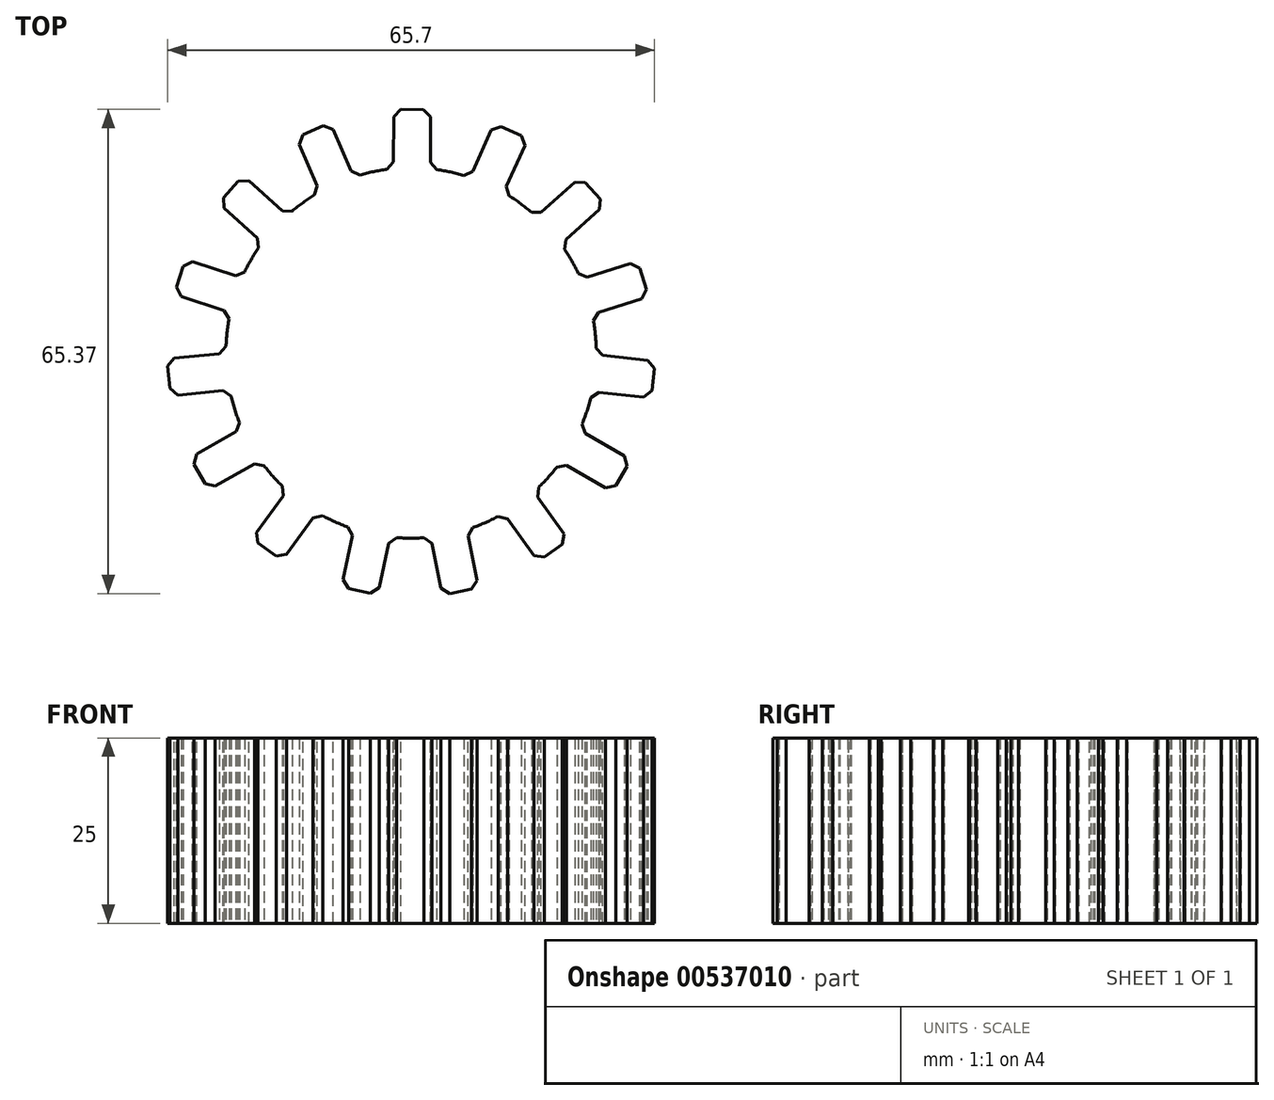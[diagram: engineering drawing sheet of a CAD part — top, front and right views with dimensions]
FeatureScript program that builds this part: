
annotation { "Feature Type Name" : "Feature", "Feature Type Description" : "" }
export const myFeature = defineFeature(function(context is Context, id is Id, definition is map)
    precondition{}
    {
        {
            var Q0;
            Q0=qCreatedBy(makeId("Top.planeOp"),FACE);
            var sketch = newSketch(context, id + "F0", { "sketchPlane" : qUnion([Q0])});
            skArc(sketch, "E0", {"start": v(22.93, 9.96) * mm, "mid": v(21.7, 12.4) * mm, "end": v(20.23, 14.7) * mm});
            skLineSegment(sketch, "E1.bottom", {"start": v(-32.46, -5.77) * mm, "end": v(-32.96, -0.8) * mm});
            skLineSegment(sketch, "E1.top", {"start": v(-24.5, -4.97) * mm, "end": v(-25, 0) * mm, "construction": true});
            skLineSegment(sketch, "E1.left", {"start": v(-32.46, -5.77) * mm, "end": v(-24.5, -4.97) * mm});
            skLineSegment(sketch, "E1.right", {"start": v(-32.96, -0.8) * mm, "end": v(-25, 0) * mm});
            skLineSegment(sketch, "E2.1.0", {"start": v(-27.3, -18.48) * mm, "end": v(-29.78, -14.14) * mm});
            skLineSegment(sketch, "E2.1.1", {"start": v(-27.3, -18.48) * mm, "end": v(-20.36, -14.5) * mm});
            skLineSegment(sketch, "E2.1.2", {"start": v(-29.78, -14.14) * mm, "end": v(-22.84, -10.17) * mm});
            skLineSegment(sketch, "E2.1.3", {"start": v(-20.36, -14.5) * mm, "end": v(-22.84, -10.17) * mm, "construction": true});
            skLineSegment(sketch, "E2.2.0", {"start": v(-17.43, -27.99) * mm, "end": v(-21.46, -25.03) * mm});
            skLineSegment(sketch, "E2.2.1", {"start": v(-17.43, -27.99) * mm, "end": v(-12.7, -21.54) * mm});
            skLineSegment(sketch, "E2.2.2", {"start": v(-21.46, -25.03) * mm, "end": v(-16.73, -18.58) * mm});
            skLineSegment(sketch, "E2.3.0", {"start": v(-4.54, -32.66) * mm, "end": v(-9.42, -31.6) * mm});
            skLineSegment(sketch, "E2.3.1", {"start": v(-4.54, -32.66) * mm, "end": v(-2.84, -24.84) * mm});
            skLineSegment(sketch, "E2.3.2", {"start": v(-9.42, -31.6) * mm, "end": v(-7.73, -23.78) * mm});
            skLineSegment(sketch, "E2.4.0", {"start": v(9.14, -31.68) * mm, "end": v(4.24, -32.7) * mm});
            skLineSegment(sketch, "E2.4.1", {"start": v(9.14, -31.68) * mm, "end": v(7.5, -23.85) * mm});
            skLineSegment(sketch, "E2.4.2", {"start": v(4.24, -32.7) * mm, "end": v(2.61, -24.86) * mm});
            skLineSegment(sketch, "E2.5.0", {"start": v(21.23, -25.22) * mm, "end": v(17.17, -28.14) * mm});
            skLineSegment(sketch, "E2.5.1", {"start": v(21.23, -25.22) * mm, "end": v(16.56, -18.73) * mm});
            skLineSegment(sketch, "E2.5.2", {"start": v(17.17, -28.14) * mm, "end": v(12.5, -21.65) * mm});
            skLineSegment(sketch, "E2.6.0", {"start": v(29.66, -14.4) * mm, "end": v(27.14, -18.73) * mm});
            skLineSegment(sketch, "E2.6.1", {"start": v(29.66, -14.4) * mm, "end": v(22.75, -10.38) * mm});
            skLineSegment(sketch, "E2.6.2", {"start": v(27.14, -18.73) * mm, "end": v(20.23, -14.7) * mm});
            skLineSegment(sketch, "E2.7.0", {"start": v(32.95, -1.1) * mm, "end": v(32.4, -6.07) * mm});
            skLineSegment(sketch, "E2.7.1", {"start": v(32.95, -1.1) * mm, "end": v(25, -0.23) * mm});
            skLineSegment(sketch, "E2.7.2", {"start": v(32.4, -6.07) * mm, "end": v(24.45, -5.2) * mm});
            skLineSegment(sketch, "E2.8.0", {"start": v(30.55, 12.4) * mm, "end": v(32.07, 7.64) * mm});
            skLineSegment(sketch, "E2.8.1", {"start": v(30.55, 12.4) * mm, "end": v(22.93, 9.96) * mm});
            skLineSegment(sketch, "E2.8.2", {"start": v(32.07, 7.64) * mm, "end": v(24.45, 5.2) * mm});
            skLineSegment(sketch, "E2.9.0", {"start": v(22.87, 23.75) * mm, "end": v(26.2, 20.02) * mm});
            skLineSegment(sketch, "E2.9.1", {"start": v(22.87, 23.75) * mm, "end": v(16.9, 18.43) * mm});
            skLineSegment(sketch, "E2.9.2", {"start": v(26.2, 20.02) * mm, "end": v(20.23, 14.7) * mm});
            skLineSegment(sketch, "E2.10.0", {"start": v(11.23, 31) * mm, "end": v(15.79, 28.94) * mm});
            skLineSegment(sketch, "E2.10.1", {"start": v(11.23, 31) * mm, "end": v(7.94, 23.7) * mm});
            skLineSegment(sketch, "E2.10.2", {"start": v(15.79, 28.94) * mm, "end": v(12.5, 21.65) * mm});
            skLineSegment(sketch, "E2.11.0", {"start": v(-2.35, 32.89) * mm, "end": v(2.65, 32.86) * mm});
            skLineSegment(sketch, "E2.11.1", {"start": v(-2.35, 32.89) * mm, "end": v(-2.39, 24.89) * mm});
            skLineSegment(sketch, "E2.11.2", {"start": v(2.65, 32.86) * mm, "end": v(2.61, 24.86) * mm});
            skLineSegment(sketch, "E2.12.0", {"start": v(-15.52, 29.09) * mm, "end": v(-10.95, 31.1) * mm});
            skLineSegment(sketch, "E2.12.1", {"start": v(-15.52, 29.09) * mm, "end": v(-12.3, 21.76) * mm});
            skLineSegment(sketch, "E2.12.2", {"start": v(-10.95, 31.1) * mm, "end": v(-7.73, 23.78) * mm});
            skLineSegment(sketch, "E2.13.0", {"start": v(-26.01, 20.26) * mm, "end": v(-22.65, 23.96) * mm});
            skLineSegment(sketch, "E2.13.1", {"start": v(-26.01, 20.26) * mm, "end": v(-20.1, 14.88) * mm});
            skLineSegment(sketch, "E2.13.2", {"start": v(-22.65, 23.96) * mm, "end": v(-16.73, 18.58) * mm});
            skLineSegment(sketch, "E2.14.0", {"start": v(-32, 7.93) * mm, "end": v(-30.44, 12.68) * mm});
            skLineSegment(sketch, "E2.14.1", {"start": v(-32, 7.93) * mm, "end": v(-24.4, 5.42) * mm});
            skLineSegment(sketch, "E2.14.2", {"start": v(-30.44, 12.68) * mm, "end": v(-22.84, 10.17) * mm});
            skArc(sketch, "E3.trimOffspring", {"start": v(16.9, 18.43) * mm, "mid": v(14.79, 20.16) * mm, "end": v(12.5, 21.65) * mm});
            skArc(sketch, "E4.trimOffspring", {"start": v(7.94, 23.7) * mm, "mid": v(5.3, 24.43) * mm, "end": v(2.61, 24.86) * mm});
            skArc(sketch, "E5.trimOffspring", {"start": v(-2.39, 24.89) * mm, "mid": v(-5.09, 24.48) * mm, "end": v(-7.73, 23.78) * mm});
            skArc(sketch, "E6.trimOffspring", {"start": v(-12.3, 21.76) * mm, "mid": v(-14.6, 20.3) * mm, "end": v(-16.73, 18.58) * mm});
            skArc(sketch, "E7.trimOffspring", {"start": v(-20.1, 14.88) * mm, "mid": v(-21.6, 12.6) * mm, "end": v(-22.84, 10.17) * mm});
            skArc(sketch, "E8.trimOffspring", {"start": v(-24.4, 5.42) * mm, "mid": v(-24.85, 2.73) * mm, "end": v(-25, 0) * mm});
            skArc(sketch, "E9.trimOffspring", {"start": v(-20.36, -14.5) * mm, "mid": v(-18.65, -16.64) * mm, "end": v(-16.73, -18.58) * mm});
            skArc(sketch, "E10.trimOffspring", {"start": v(-12.7, -21.54) * mm, "mid": v(-10.27, -22.8) * mm, "end": v(-7.73, -23.78) * mm});
            skArc(sketch, "E11.trimOffspring", {"start": v(-2.84, -24.84) * mm, "mid": v(-0.11, -25) * mm, "end": v(2.61, -24.86) * mm});
            skArc(sketch, "E12.trimOffspring", {"start": v(7.5, -23.85) * mm, "mid": v(10.06, -22.88) * mm, "end": v(12.5, -21.65) * mm});
            skArc(sketch, "E13.trimOffspring", {"start": v(16.56, -18.73) * mm, "mid": v(18.5, -16.81) * mm, "end": v(20.23, -14.7) * mm});
            skArc(sketch, "E14.trimOffspring", {"start": v(22.75, -10.38) * mm, "mid": v(23.74, -7.83) * mm, "end": v(24.45, -5.2) * mm});
            skArc(sketch, "E15.trimOffspring", {"start": v(25, -0.23) * mm, "mid": v(24.87, 2.5) * mm, "end": v(24.45, 5.2) * mm});
            skArc(sketch, "E16.trimOffspring", {"start": v(-24.5, -4.97) * mm, "mid": v(-23.81, -7.62) * mm, "end": v(-22.84, -10.17) * mm});
            skSolve(sketch);
        }
        {
            var Q0;
            Q0=makeQuery(id+"F0.imprint","IMPRINT",FACE,{"disambiguationData":[TD([[makeQuery(id+"F0.imprint","IMPRINT",EDGE,{"derivedFrom":sQuery(id+"F0.wireOp",EDGE,"E0")}),1.0]])]});
            extrude(context, id + "F1", {"entities" : qUnion([Q0]), "depth" : 25 * mm, "offsetDistance" : 25 * mm});
        }
        {
            var Q0;
            Q0=makeQuery(id+"F1.opExtrude","SWEPT_EDGE",EDGE,{"disambiguationData":[OSD([sQuery(id+"F0.wireOp",EDGE,"E2.1.0"),sQuery(id+"F0.wireOp",EDGE,"E2.1.1")])]});
            var Q1;
            Q1=makeQuery(id+"F1.opExtrude","SWEPT_EDGE",EDGE,{"disambiguationData":[OSD([sQuery(id+"F0.wireOp",EDGE,"E2.2.0"),sQuery(id+"F0.wireOp",EDGE,"E2.2.1")])]});
            var Q2;
            Q2=makeQuery(id+"F1.opExtrude","SWEPT_EDGE",EDGE,{"disambiguationData":[OSD([sQuery(id+"F0.wireOp",EDGE,"E2.3.0"),sQuery(id+"F0.wireOp",EDGE,"E2.3.1")])]});
            var Q3;
            Q3=makeQuery(id+"F1.opExtrude","SWEPT_EDGE",EDGE,{"disambiguationData":[OSD([sQuery(id+"F0.wireOp",EDGE,"E2.4.0"),sQuery(id+"F0.wireOp",EDGE,"E2.4.1")])]});
            var Q4;
            Q4=makeQuery(id+"F1.opExtrude","SWEPT_EDGE",EDGE,{"disambiguationData":[OSD([sQuery(id+"F0.wireOp",EDGE,"E2.4.0"),sQuery(id+"F0.wireOp",EDGE,"E2.4.2")])]});
            var Q5;
            Q5=makeQuery(id+"F1.opExtrude","SWEPT_EDGE",EDGE,{"disambiguationData":[OSD([sQuery(id+"F0.wireOp",EDGE,"E2.3.0"),sQuery(id+"F0.wireOp",EDGE,"E2.3.2")])]});
            var Q6;
            Q6=makeQuery(id+"F1.opExtrude","SWEPT_EDGE",EDGE,{"disambiguationData":[OSD([sQuery(id+"F0.wireOp",EDGE,"E2.2.0"),sQuery(id+"F0.wireOp",EDGE,"E2.2.2")])]});
            var Q7;
            Q7=makeQuery(id+"F1.opExtrude","SWEPT_EDGE",EDGE,{"disambiguationData":[OSD([sQuery(id+"F0.wireOp",EDGE,"E2.5.0"),sQuery(id+"F0.wireOp",EDGE,"E2.5.2")])]});
            var Q8;
            Q8=makeQuery(id+"F1.opExtrude","SWEPT_EDGE",EDGE,{"disambiguationData":[OSD([sQuery(id+"F0.wireOp",EDGE,"E2.5.0"),sQuery(id+"F0.wireOp",EDGE,"E2.5.1")])]});
            var Q9;
            Q9=makeQuery(id+"F1.opExtrude","SWEPT_EDGE",EDGE,{"disambiguationData":[OSD([sQuery(id+"F0.wireOp",EDGE,"E2.6.0"),sQuery(id+"F0.wireOp",EDGE,"E2.6.2")])]});
            var Q10;
            Q10=makeQuery(id+"F1.opExtrude","SWEPT_EDGE",EDGE,{"disambiguationData":[OSD([sQuery(id+"F0.wireOp",EDGE,"E2.6.0"),sQuery(id+"F0.wireOp",EDGE,"E2.6.1")])]});
            var Q11;
            Q11=makeQuery(id+"F1.opExtrude","SWEPT_EDGE",EDGE,{"disambiguationData":[OSD([sQuery(id+"F0.wireOp",EDGE,"E2.7.0"),sQuery(id+"F0.wireOp",EDGE,"E2.7.2")])]});
            var Q12;
            Q12=makeQuery(id+"F1.opExtrude","SWEPT_EDGE",EDGE,{"disambiguationData":[OSD([sQuery(id+"F0.wireOp",EDGE,"E2.7.0"),sQuery(id+"F0.wireOp",EDGE,"E2.7.1")])]});
            var Q13;
            Q13=makeQuery(id+"F1.opExtrude","SWEPT_EDGE",EDGE,{"disambiguationData":[OSD([sQuery(id+"F0.wireOp",EDGE,"E2.8.0"),sQuery(id+"F0.wireOp",EDGE,"E2.8.2")])]});
            var Q14;
            Q14=makeQuery(id+"F1.opExtrude","SWEPT_EDGE",EDGE,{"disambiguationData":[OSD([sQuery(id+"F0.wireOp",EDGE,"E2.8.0"),sQuery(id+"F0.wireOp",EDGE,"E2.8.1")])]});
            var Q15;
            Q15=makeQuery(id+"F1.opExtrude","SWEPT_EDGE",EDGE,{"disambiguationData":[OSD([sQuery(id+"F0.wireOp",EDGE,"E2.9.0"),sQuery(id+"F0.wireOp",EDGE,"E2.9.2")])]});
            var Q16;
            Q16=makeQuery(id+"F1.opExtrude","SWEPT_EDGE",EDGE,{"disambiguationData":[OSD([sQuery(id+"F0.wireOp",EDGE,"E2.9.0"),sQuery(id+"F0.wireOp",EDGE,"E2.9.1")])]});
            var Q17;
            Q17=makeQuery(id+"F1.opExtrude","SWEPT_EDGE",EDGE,{"disambiguationData":[OSD([sQuery(id+"F0.wireOp",EDGE,"E2.10.0"),sQuery(id+"F0.wireOp",EDGE,"E2.10.2")])]});
            var Q18;
            Q18=makeQuery(id+"F1.opExtrude","SWEPT_EDGE",EDGE,{"disambiguationData":[OSD([sQuery(id+"F0.wireOp",EDGE,"E2.10.0"),sQuery(id+"F0.wireOp",EDGE,"E2.10.1")])]});
            var Q19;
            Q19=makeQuery(id+"F1.opExtrude","SWEPT_EDGE",EDGE,{"disambiguationData":[OSD([sQuery(id+"F0.wireOp",EDGE,"E2.11.0"),sQuery(id+"F0.wireOp",EDGE,"E2.11.2")])]});
            var Q20;
            Q20=makeQuery(id+"F1.opExtrude","SWEPT_EDGE",EDGE,{"disambiguationData":[OSD([sQuery(id+"F0.wireOp",EDGE,"E2.11.0"),sQuery(id+"F0.wireOp",EDGE,"E2.11.1")])]});
            var Q21;
            Q21=makeQuery(id+"F1.opExtrude","SWEPT_EDGE",EDGE,{"disambiguationData":[OSD([sQuery(id+"F0.wireOp",EDGE,"E2.12.0"),sQuery(id+"F0.wireOp",EDGE,"E2.12.2")])]});
            var Q22;
            Q22=makeQuery(id+"F1.opExtrude","SWEPT_EDGE",EDGE,{"disambiguationData":[OSD([sQuery(id+"F0.wireOp",EDGE,"E2.12.0"),sQuery(id+"F0.wireOp",EDGE,"E2.12.1")])]});
            var Q23;
            Q23=makeQuery(id+"F1.opExtrude","SWEPT_EDGE",EDGE,{"disambiguationData":[OSD([sQuery(id+"F0.wireOp",EDGE,"E2.13.0"),sQuery(id+"F0.wireOp",EDGE,"E2.13.2")])]});
            var Q24;
            Q24=makeQuery(id+"F1.opExtrude","SWEPT_EDGE",EDGE,{"disambiguationData":[OSD([sQuery(id+"F0.wireOp",EDGE,"E2.13.0"),sQuery(id+"F0.wireOp",EDGE,"E2.13.1")])]});
            var Q25;
            Q25=makeQuery(id+"F1.opExtrude","SWEPT_EDGE",EDGE,{"disambiguationData":[OSD([sQuery(id+"F0.wireOp",EDGE,"E2.14.0"),sQuery(id+"F0.wireOp",EDGE,"E2.14.2")])]});
            var Q26;
            Q26=makeQuery(id+"F1.opExtrude","SWEPT_EDGE",EDGE,{"disambiguationData":[OSD([sQuery(id+"F0.wireOp",EDGE,"E2.14.0"),sQuery(id+"F0.wireOp",EDGE,"E2.14.1")])]});
            var Q27;
            Q27=makeQuery(id+"F1.opExtrude","SWEPT_EDGE",EDGE,{"disambiguationData":[OSD([sQuery(id+"F0.wireOp",EDGE,"E1.bottom"),sQuery(id+"F0.wireOp",EDGE,"E1.right")])]});
            var Q28;
            Q28=makeQuery(id+"F1.opExtrude","SWEPT_EDGE",EDGE,{"disambiguationData":[OSD([sQuery(id+"F0.wireOp",EDGE,"E1.bottom"),sQuery(id+"F0.wireOp",EDGE,"E1.left")])]});
            var Q29;
            Q29=makeQuery(id+"F1.opExtrude","SWEPT_EDGE",EDGE,{"disambiguationData":[OSD([sQuery(id+"F0.wireOp",EDGE,"E2.1.0"),sQuery(id+"F0.wireOp",EDGE,"E2.1.2")])]});
            chamfer(context, id + "F2", {"entities" : qUnion([Q0, Q1, Q2, Q3, Q4, Q5, Q6, Q7, Q8, Q9, Q10, Q11, Q12, Q13, Q14, Q15, Q16, Q17, Q18, Q19, Q20, Q21, Q22, Q23, Q24, Q25, Q26, Q27, Q28, Q29]), "width" : 1 * mm, "tangentPropagation" : true});
        }
        {
            var Q0;
            Q0=makeQuery(id+"F1.opExtrude","SWEPT_EDGE",EDGE,{"disambiguationData":[OSD([sQuery(id+"F0.wireOp",EDGE,"E2.8.2"),sQuery(id+"F0.wireOp",EDGE,"E15.trimOffspring")])]});
            var Q1;
            Q1=makeQuery(id+"F1.opExtrude","SWEPT_EDGE",EDGE,{"disambiguationData":[OSD([sQuery(id+"F0.wireOp",EDGE,"E0"),sQuery(id+"F0.wireOp",EDGE,"E2.9.2")])]});
            var Q2;
            Q2=makeQuery(id+"F1.opExtrude","SWEPT_EDGE",EDGE,{"disambiguationData":[OSD([sQuery(id+"F0.wireOp",EDGE,"E2.10.2"),sQuery(id+"F0.wireOp",EDGE,"E3.trimOffspring")])]});
            var Q3;
            Q3=makeQuery(id+"F1.opExtrude","SWEPT_EDGE",EDGE,{"disambiguationData":[OSD([sQuery(id+"F0.wireOp",EDGE,"E2.11.2"),sQuery(id+"F0.wireOp",EDGE,"E4.trimOffspring")])]});
            var Q4;
            Q4=makeQuery(id+"F1.opExtrude","SWEPT_EDGE",EDGE,{"disambiguationData":[OSD([sQuery(id+"F0.wireOp",EDGE,"E2.12.2"),sQuery(id+"F0.wireOp",EDGE,"E5.trimOffspring")])]});
            var Q5;
            Q5=makeQuery(id+"F1.opExtrude","SWEPT_EDGE",EDGE,{"disambiguationData":[OSD([sQuery(id+"F0.wireOp",EDGE,"E2.13.2"),sQuery(id+"F0.wireOp",EDGE,"E6.trimOffspring")])]});
            var Q6;
            Q6=makeQuery(id+"F1.opExtrude","SWEPT_EDGE",EDGE,{"disambiguationData":[OSD([sQuery(id+"F0.wireOp",EDGE,"E2.14.2"),sQuery(id+"F0.wireOp",EDGE,"E7.trimOffspring")])]});
            var Q7;
            Q7=makeQuery(id+"F1.opExtrude","SWEPT_EDGE",EDGE,{"disambiguationData":[OSD([sQuery(id+"F0.wireOp",EDGE,"E1.right"),sQuery(id+"F0.wireOp",EDGE,"E8.trimOffspring")])]});
            var Q8;
            Q8=makeQuery(id+"F1.opExtrude","SWEPT_EDGE",EDGE,{"disambiguationData":[OSD([sQuery(id+"F0.wireOp",EDGE,"E2.1.2"),sQuery(id+"F0.wireOp",EDGE,"E16.trimOffspring")])]});
            var Q9;
            Q9=makeQuery(id+"F1.opExtrude","SWEPT_EDGE",EDGE,{"disambiguationData":[OSD([sQuery(id+"F0.wireOp",EDGE,"E1.left"),sQuery(id+"F0.wireOp",EDGE,"E16.trimOffspring")])]});
            var Q10;
            Q10=makeQuery(id+"F1.opExtrude","SWEPT_EDGE",EDGE,{"disambiguationData":[OSD([sQuery(id+"F0.wireOp",EDGE,"E2.14.1"),sQuery(id+"F0.wireOp",EDGE,"E8.trimOffspring")])]});
            var Q11;
            Q11=makeQuery(id+"F1.opExtrude","SWEPT_EDGE",EDGE,{"disambiguationData":[OSD([sQuery(id+"F0.wireOp",EDGE,"E2.13.1"),sQuery(id+"F0.wireOp",EDGE,"E7.trimOffspring")])]});
            var Q12;
            Q12=makeQuery(id+"F1.opExtrude","SWEPT_EDGE",EDGE,{"disambiguationData":[OSD([sQuery(id+"F0.wireOp",EDGE,"E2.1.1"),sQuery(id+"F0.wireOp",EDGE,"E9.trimOffspring")])]});
            var Q13;
            Q13=makeQuery(id+"F1.opExtrude","SWEPT_EDGE",EDGE,{"disambiguationData":[OSD([sQuery(id+"F0.wireOp",EDGE,"E2.2.2"),sQuery(id+"F0.wireOp",EDGE,"E9.trimOffspring")])]});
            var Q14;
            Q14=makeQuery(id+"F1.opExtrude","SWEPT_EDGE",EDGE,{"disambiguationData":[OSD([sQuery(id+"F0.wireOp",EDGE,"E2.2.1"),sQuery(id+"F0.wireOp",EDGE,"E10.trimOffspring")])]});
            var Q15;
            Q15=makeQuery(id+"F1.opExtrude","SWEPT_EDGE",EDGE,{"disambiguationData":[OSD([sQuery(id+"F0.wireOp",EDGE,"E2.3.2"),sQuery(id+"F0.wireOp",EDGE,"E10.trimOffspring")])]});
            var Q16;
            Q16=makeQuery(id+"F1.opExtrude","SWEPT_EDGE",EDGE,{"disambiguationData":[OSD([sQuery(id+"F0.wireOp",EDGE,"E2.4.2"),sQuery(id+"F0.wireOp",EDGE,"E11.trimOffspring")])]});
            var Q17;
            Q17=makeQuery(id+"F1.opExtrude","SWEPT_EDGE",EDGE,{"disambiguationData":[OSD([sQuery(id+"F0.wireOp",EDGE,"E2.3.1"),sQuery(id+"F0.wireOp",EDGE,"E11.trimOffspring")])]});
            var Q18;
            Q18=makeQuery(id+"F1.opExtrude","SWEPT_EDGE",EDGE,{"disambiguationData":[OSD([sQuery(id+"F0.wireOp",EDGE,"E2.5.2"),sQuery(id+"F0.wireOp",EDGE,"E12.trimOffspring")])]});
            var Q19;
            Q19=makeQuery(id+"F1.opExtrude","SWEPT_EDGE",EDGE,{"disambiguationData":[OSD([sQuery(id+"F0.wireOp",EDGE,"E2.4.1"),sQuery(id+"F0.wireOp",EDGE,"E12.trimOffspring")])]});
            var Q20;
            Q20=makeQuery(id+"F1.opExtrude","SWEPT_EDGE",EDGE,{"disambiguationData":[OSD([sQuery(id+"F0.wireOp",EDGE,"E2.5.1"),sQuery(id+"F0.wireOp",EDGE,"E13.trimOffspring")])]});
            var Q21;
            Q21=makeQuery(id+"F1.opExtrude","SWEPT_EDGE",EDGE,{"disambiguationData":[OSD([sQuery(id+"F0.wireOp",EDGE,"E2.6.2"),sQuery(id+"F0.wireOp",EDGE,"E13.trimOffspring")])]});
            var Q22;
            Q22=makeQuery(id+"F1.opExtrude","SWEPT_EDGE",EDGE,{"disambiguationData":[OSD([sQuery(id+"F0.wireOp",EDGE,"E2.6.1"),sQuery(id+"F0.wireOp",EDGE,"E14.trimOffspring")])]});
            var Q23;
            Q23=makeQuery(id+"F1.opExtrude","SWEPT_EDGE",EDGE,{"disambiguationData":[OSD([sQuery(id+"F0.wireOp",EDGE,"E2.7.2"),sQuery(id+"F0.wireOp",EDGE,"E14.trimOffspring")])]});
            var Q24;
            Q24=makeQuery(id+"F1.opExtrude","SWEPT_EDGE",EDGE,{"disambiguationData":[OSD([sQuery(id+"F0.wireOp",EDGE,"E2.7.1"),sQuery(id+"F0.wireOp",EDGE,"E15.trimOffspring")])]});
            var Q25;
            Q25=makeQuery(id+"F1.opExtrude","SWEPT_EDGE",EDGE,{"disambiguationData":[OSD([sQuery(id+"F0.wireOp",EDGE,"E0"),sQuery(id+"F0.wireOp",EDGE,"E2.8.1")])]});
            var Q26;
            Q26=makeQuery(id+"F1.opExtrude","SWEPT_EDGE",EDGE,{"disambiguationData":[OSD([sQuery(id+"F0.wireOp",EDGE,"E2.9.1"),sQuery(id+"F0.wireOp",EDGE,"E3.trimOffspring")])]});
            var Q27;
            Q27=makeQuery(id+"F1.opExtrude","SWEPT_EDGE",EDGE,{"disambiguationData":[OSD([sQuery(id+"F0.wireOp",EDGE,"E2.10.1"),sQuery(id+"F0.wireOp",EDGE,"E4.trimOffspring")])]});
            var Q28;
            Q28=makeQuery(id+"F1.opExtrude","SWEPT_EDGE",EDGE,{"disambiguationData":[OSD([sQuery(id+"F0.wireOp",EDGE,"E2.11.1"),sQuery(id+"F0.wireOp",EDGE,"E5.trimOffspring")])]});
            var Q29;
            Q29=makeQuery(id+"F1.opExtrude","SWEPT_EDGE",EDGE,{"disambiguationData":[OSD([sQuery(id+"F0.wireOp",EDGE,"E2.12.1"),sQuery(id+"F0.wireOp",EDGE,"E6.trimOffspring")])]});
            chamfer(context, id + "F3", {"entities" : qUnion([Q0, Q1, Q2, Q3, Q4, Q5, Q6, Q7, Q8, Q9, Q10, Q11, Q12, Q13, Q14, Q15, Q16, Q17, Q18, Q19, Q20, Q21, Q22, Q23, Q24, Q25, Q26, Q27, Q28, Q29]), "width" : 1 * mm, "tangentPropagation" : true});
        }
    });
